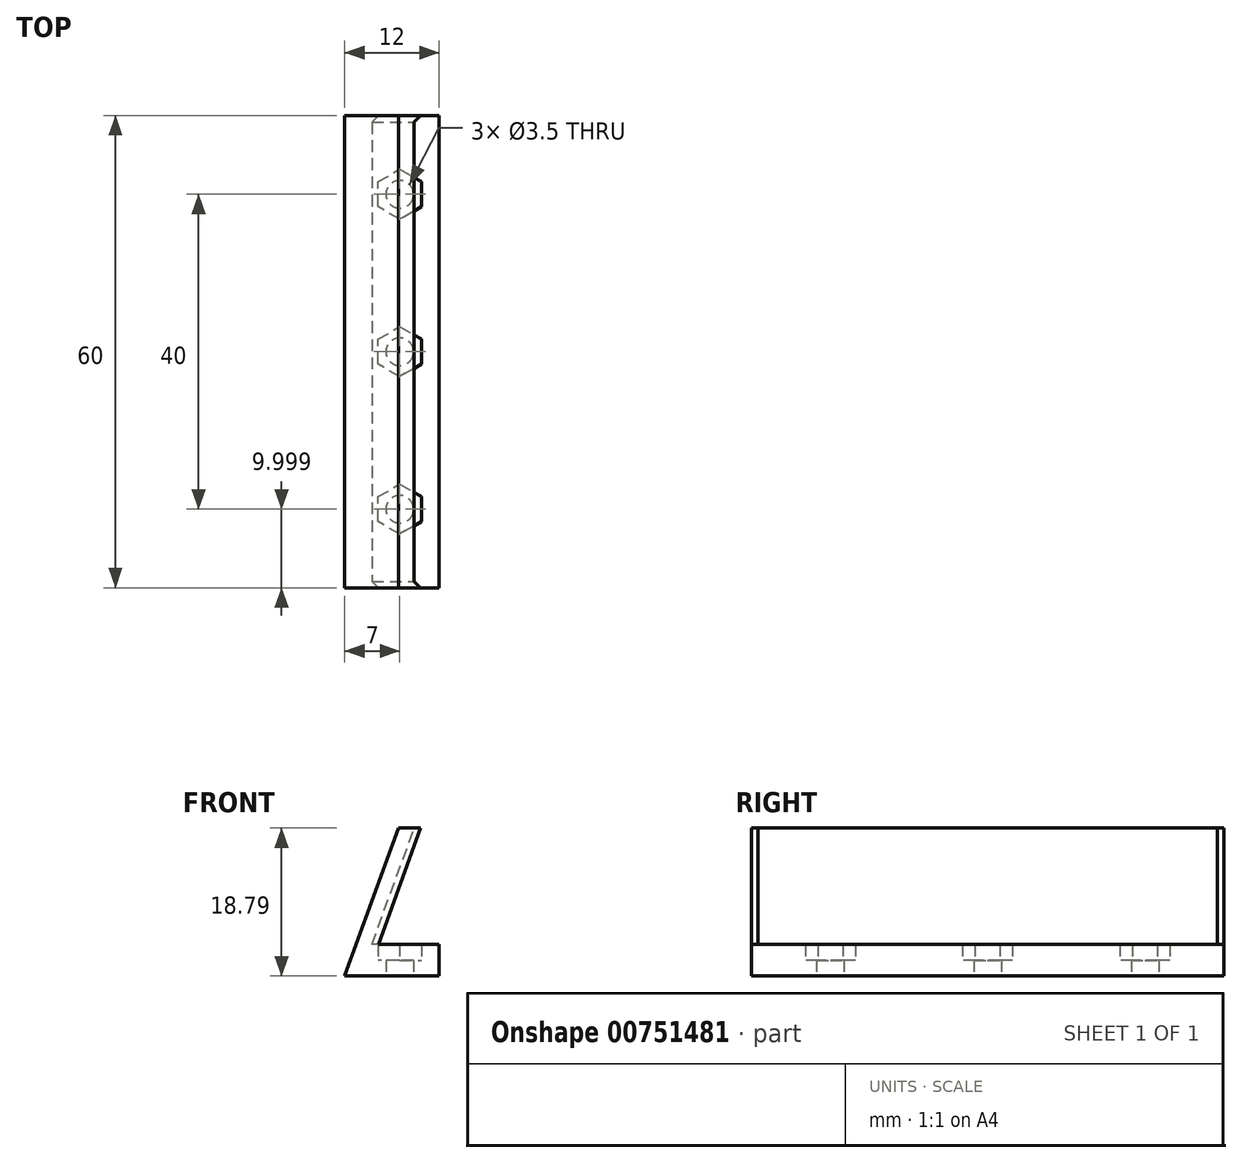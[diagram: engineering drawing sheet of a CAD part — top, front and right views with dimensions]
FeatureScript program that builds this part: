
annotation { "Feature Type Name" : "Feature", "Feature Type Description" : "" }
export const myFeature = defineFeature(function(context is Context, id is Id, definition is map)
    precondition{}
    {
        {
            var Q0;
            Q0=qCreatedBy(makeId("Top.planeOp"),FACE);
            var sketch = newSketch(context, id + "F0", { "sketchPlane" : qUnion([Q0])});
            skLineSegment(sketch, "E0.left", {"start": v(-20, 33.58) * mm, "end": v(-20, -26.42) * mm});
            skLineSegment(sketch, "E1", {"start": v(-20, 33.58) * mm, "end": v(0, 53.58) * mm});
            skLineSegment(sketch, "E2", {"start": v(-20, -26.42) * mm, "end": v(0, -46.42) * mm});
            skLineSegment(sketch, "E3.bottom", {"start": v(-20, 33.58) * mm, "end": v(-8, 33.58) * mm});
            skLineSegment(sketch, "E3.top", {"start": v(-20, -26.42) * mm, "end": v(-8, -26.42) * mm});
            skLineSegment(sketch, "E3.right", {"start": v(-8, 33.58) * mm, "end": v(-8, -26.42) * mm});
            skLineSegment(sketch, "E4.0", {"start": v(-18, 32.75) * mm, "end": v(2.3, 53.04) * mm});
            skLineSegment(sketch, "E4.1", {"start": v(-18, 32.75) * mm, "end": v(-18, -25.6) * mm});
            skLineSegment(sketch, "E4.2", {"start": v(-18, -25.6) * mm, "end": v(0.53, -44.13) * mm});
            skCircle(sketch, "E5", {"center": v(-13, 23.58) * mm, "radius": 1.75 * mm});
            skCircle(sketch, "E6", {"center": v(-13, 3.58) * mm, "radius": 1.75 * mm});
            skCircle(sketch, "E7", {"center": v(-13, -16.42) * mm, "radius": 1.75 * mm});
            skCircle(sketch, "E8.cCircle", {"center": v(-13, 23.58) * mm, "radius": 2.75 * mm, "construction": true});
            skLineSegment(sketch, "E8.0", {"start": v(-10.25, 25.17) * mm, "end": v(-10.25, 22) * mm});
            skLineSegment(sketch, "E8.1", {"start": v(-10.25, 22) * mm, "end": v(-13, 20.4) * mm});
            skLineSegment(sketch, "E8.2", {"start": v(-13, 20.4) * mm, "end": v(-15.75, 22) * mm});
            skLineSegment(sketch, "E8.3", {"start": v(-15.75, 22) * mm, "end": v(-15.75, 25.17) * mm});
            skLineSegment(sketch, "E8.4", {"start": v(-15.75, 25.17) * mm, "end": v(-13, 26.75) * mm});
            skLineSegment(sketch, "E8.5", {"start": v(-13, 26.75) * mm, "end": v(-10.25, 25.17) * mm});
            skPoint(sketch, "E8.0.midPoint", {"position": v(-10.25, 23.58) * mm});
            skCircle(sketch, "E9.cCircle", {"center": v(-13, 3.58) * mm, "radius": 2.75 * mm, "construction": true});
            skLineSegment(sketch, "E9.0", {"start": v(-10.25, 5.17) * mm, "end": v(-10.25, 2) * mm});
            skLineSegment(sketch, "E9.1", {"start": v(-10.25, 2) * mm, "end": v(-13, 0.4) * mm});
            skLineSegment(sketch, "E9.2", {"start": v(-13, 0.4) * mm, "end": v(-15.75, 2) * mm});
            skLineSegment(sketch, "E9.3", {"start": v(-15.75, 2) * mm, "end": v(-15.75, 5.17) * mm});
            skLineSegment(sketch, "E9.4", {"start": v(-15.75, 5.17) * mm, "end": v(-13, 6.75) * mm});
            skLineSegment(sketch, "E9.5", {"start": v(-13, 6.75) * mm, "end": v(-10.25, 5.17) * mm});
            skPoint(sketch, "E9.0.midPoint", {"position": v(-10.25, 3.58) * mm});
            skCircle(sketch, "E10.cCircle", {"center": v(-13, -16.42) * mm, "radius": 2.75 * mm, "construction": true});
            skLineSegment(sketch, "E10.0", {"start": v(-10.25, -14.83) * mm, "end": v(-10.25, -18) * mm});
            skLineSegment(sketch, "E10.1", {"start": v(-10.25, -18) * mm, "end": v(-13, -19.6) * mm});
            skLineSegment(sketch, "E10.2", {"start": v(-13, -19.6) * mm, "end": v(-15.75, -18) * mm});
            skLineSegment(sketch, "E10.3", {"start": v(-15.75, -18) * mm, "end": v(-15.75, -14.83) * mm});
            skLineSegment(sketch, "E10.4", {"start": v(-15.75, -14.83) * mm, "end": v(-13, -13.25) * mm});
            skLineSegment(sketch, "E10.5", {"start": v(-13, -13.25) * mm, "end": v(-10.25, -14.83) * mm});
            skPoint(sketch, "E10.0.midPoint", {"position": v(-10.25, -16.42) * mm});
            skLineSegment(sketch, "E11", {"start": v(-13, 23.58) * mm, "end": v(-13, 33.58) * mm, "construction": true});
            skLineSegment(sketch, "E12", {"start": v(-13, 23.58) * mm, "end": v(-13, 3.58) * mm, "construction": true});
            skLineSegment(sketch, "E13", {"start": v(-13, 3.58) * mm, "end": v(-13, -16.42) * mm, "construction": true});
            skLineSegment(sketch, "E14", {"start": v(-13, -16.42) * mm, "end": v(-13, -26.42) * mm, "construction": true});
            skSolve(sketch);
        }
        {
            var Q0;
            Q0=qCreatedBy(makeId("Front.planeOp"),FACE);
            var sketch = newSketch(context, id + "F1", { "sketchPlane" : qUnion([Q0])});
            skLineSegment(sketch, "E15", {"start": v(0, 0) * mm, "end": v(6.84, 18.8) * mm});
            skSolve(sketch);
        }
        {
            var Q0;
            {var subQ1=sQuery(id+"F0.wireOp",EDGE,"E0.left");Q0=makeQuery(id+"F0.imprint","IMPRINT",FACE,{"disambiguationData":[TD([[makeQuery(id+"F0.imprint","IMPRINT",EDGE,{"derivedFrom":subQ1}),1.0]])]});}
            var Q1;
            Q1=sQuery(id+"F1.wireOp",EDGE,"E15");
            sweep(context, id + "F2", {"profiles" : qUnion([Q0]), "path" : qUnion([Q1])});
        }
        {
            var Q0;
            {var subQ4=sQuery(id+"F0.wireOp",EDGE,"E3.right");Q0=makeQuery(id+"F0.imprint","IMPRINT",FACE,{"disambiguationData":[TD([[makeQuery(id+"F0.imprint","IMPRINT",EDGE,{"derivedFrom":subQ4}),-1.0]])]});}
            extrude(context, id + "F3", {"entities" : qUnion([Q0]), "operationType" : NewBodyOperationType.ADD, "depth" : 4 * mm, "offsetDistance" : 25 * mm});
        }
        {
            var Q0;
            Q0=makeQuery(id+"F0.imprint","IMPRINT",FACE,{"disambiguationData":[TD([[makeQuery(id+"F0.imprint","IMPRINT",EDGE,{"derivedFrom":sQuery(id+"F0.wireOp",EDGE,"E5")}),-1.0]])]});
            var Q1;
            Q1=makeQuery(id+"F0.imprint","IMPRINT",FACE,{"disambiguationData":[TD([[makeQuery(id+"F0.imprint","IMPRINT",EDGE,{"derivedFrom":sQuery(id+"F0.wireOp",EDGE,"E6")}),-1.0]])]});
            var Q2;
            Q2=makeQuery(id+"F0.imprint","IMPRINT",FACE,{"disambiguationData":[TD([[makeQuery(id+"F0.imprint","IMPRINT",EDGE,{"derivedFrom":sQuery(id+"F0.wireOp",EDGE,"E7")}),-1.0]])]});
            extrude(context, id + "F4", {"entities" : qUnion([Q0, Q1, Q2]), "operationType" : NewBodyOperationType.ADD, "depth" : 2 * mm, "offsetDistance" : 25 * mm});
        }
    });
